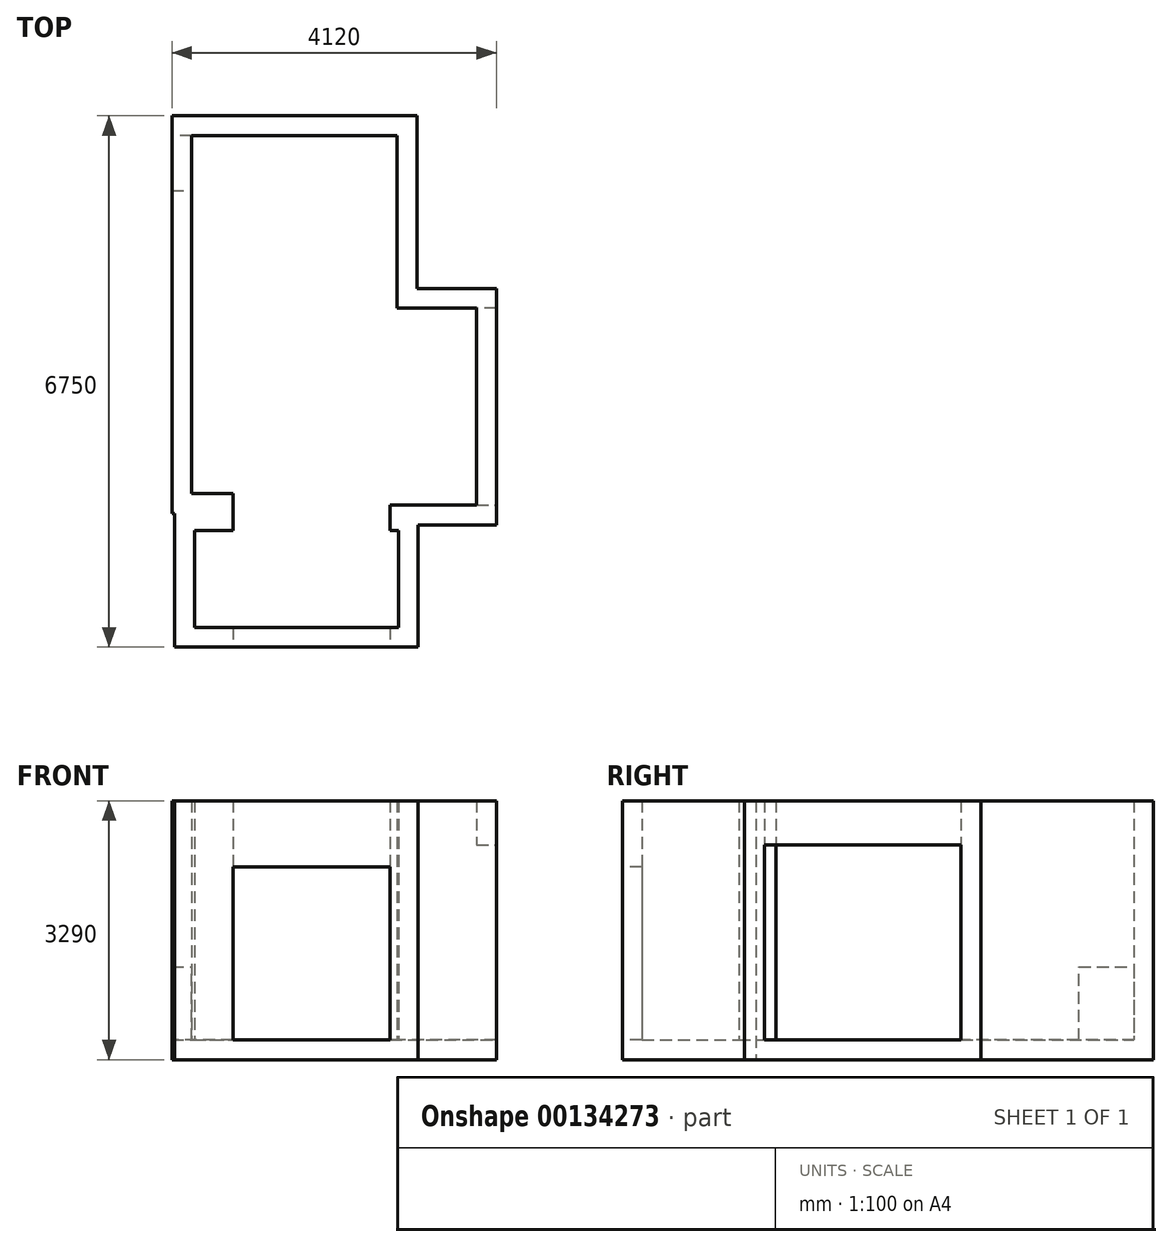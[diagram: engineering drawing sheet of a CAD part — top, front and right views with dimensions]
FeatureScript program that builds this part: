
annotation { "Feature Type Name" : "Feature", "Feature Type Description" : "" }
export const myFeature = defineFeature(function(context is Context, id is Id, definition is map)
    precondition{}
    {
        {
            var Q0;
            Q0=qCreatedBy(makeId("Top.planeOp"),FACE);
            var sketch = newSketch(context, id + "F0", { "sketchPlane" : qUnion([Q0])});
            skLineSegment(sketch, "E0", {"start": v(0, 0) * mm, "end": v(1649.99, 0) * mm});
            skLineSegment(sketch, "E1", {"start": v(1649.99, 0) * mm, "end": v(1649.99, 1230) * mm});
            skLineSegment(sketch, "E2", {"start": v(1649.99, 1230) * mm, "end": v(1544.99, 1230) * mm});
            skLineSegment(sketch, "E3", {"start": v(1544.99, 1230) * mm, "end": v(1544.99, 1555) * mm});
            skLineSegment(sketch, "E4", {"start": v(1544.99, 1555) * mm, "end": v(2644.99, 1555) * mm});
            skLineSegment(sketch, "E5", {"start": v(2644.99, 1555) * mm, "end": v(2644.99, 4055) * mm});
            skLineSegment(sketch, "E6", {"start": v(2644.99, 4055) * mm, "end": v(1634.99, 4055) * mm});
            skLineSegment(sketch, "E7", {"start": v(1634.99, 4055) * mm, "end": v(1634.99, 6250) * mm});
            skLineSegment(sketch, "E8", {"start": v(1634.99, 6250) * mm, "end": v(-975.01, 6250) * mm});
            skLineSegment(sketch, "E9", {"start": v(-975.01, 6250) * mm, "end": v(-975.01, 1700) * mm});
            skLineSegment(sketch, "E10", {"start": v(-975.01, 1700) * mm, "end": v(-450.01, 1700) * mm});
            skLineSegment(sketch, "E11", {"start": v(-450.01, 1700) * mm, "end": v(-450.01, 1230) * mm});
            skLineSegment(sketch, "E12", {"start": v(-450.01, 1230) * mm, "end": v(-940.01, 1230) * mm});
            skLineSegment(sketch, "E13", {"start": v(-940.01, 1230) * mm, "end": v(-940.01, 0) * mm});
            skLineSegment(sketch, "E14", {"start": v(-940.01, 0) * mm, "end": v(0, 0) * mm});
            skSolve(sketch);
        }
        {
            var Q0;
            Q0 = qSketchRegion(id + "F0", true);
            extrude(context, id + "F1", {"entities" : qUnion([Q0]), "depth" : 3040 * mm});
        }
        {
            var Q0;
            Q0=makeQuery(id+"F1.opExtrude","CAP_FACE",FACE,{"disambiguationData":[OSD([sQuery(id+"F0.wireOp",EDGE,"E0"),sQuery(id+"F0.wireOp",EDGE,"E1"),sQuery(id+"F0.wireOp",EDGE,"E2"),sQuery(id+"F0.wireOp",EDGE,"E3"),sQuery(id+"F0.wireOp",EDGE,"E4"),sQuery(id+"F0.wireOp",EDGE,"E5"),sQuery(id+"F0.wireOp",EDGE,"E6"),sQuery(id+"F0.wireOp",EDGE,"E7"),sQuery(id+"F0.wireOp",EDGE,"E8"),sQuery(id+"F0.wireOp",EDGE,"E9"),sQuery(id+"F0.wireOp",EDGE,"E10"),sQuery(id+"F0.wireOp",EDGE,"E11"),sQuery(id+"F0.wireOp",EDGE,"E12"),sQuery(id+"F0.wireOp",EDGE,"E13"),sQuery(id+"F0.wireOp",EDGE,"E14")])],"isStart":false});
            shell(context, id + "F2", {"entities" : qUnion([Q0]), "thickness" : 250 * mm, "oppositeDirection" : true});
        }
        {
            var Q0;
            Q0=makeQuery(id+"F2.opShell","OFFSET_FACE",FACE,{"disambiguationData":[OSD([sQuery(id+"F0.wireOp",EDGE,"E5")])]});
            var sketch = newSketch(context, id + "F3", { "sketchPlane" : qUnion([Q0])});
            skLineSegment(sketch, "E15.bottom", {"start": v(-3330, 1705) * mm, "end": v(-2620, 1705) * mm});
            skLineSegment(sketch, "E15.top", {"start": v(-3330, 980) * mm, "end": v(-2620, 980) * mm});
            skLineSegment(sketch, "E15.left", {"start": v(-3330, 1705) * mm, "end": v(-3330, 980) * mm});
            skLineSegment(sketch, "E15.right", {"start": v(-2620, 1705) * mm, "end": v(-2620, 980) * mm});
            skSolve(sketch);
        }
        {
            var Q0;
            Q0 = qSketchRegion(id + "F3", true);
            extrude(context, id + "F4", {"entities" : qUnion([Q0]), "operationType" : NewBodyOperationType.REMOVE, "endBound" : BoundingType.THROUGH_ALL, "oppositeDirection" : true, "depth" : 20 * mm});
        }
        {
            var Q0;
            Q0=makeQuery(id+"F1.opExtrude","SWEPT_FACE",FACE,{"disambiguationData":[OSD([sQuery(id+"F0.wireOp",EDGE,"E0"),sQuery(id+"F0.wireOp",EDGE,"E14")])]});
            var sketch = newSketch(context, id + "F5", { "sketchPlane" : qUnion([Q0])});
            skLineSegment(sketch, "E16.bottom", {"start": v(-450.01, 0) * mm, "end": v(1544.99, 0) * mm});
            skLineSegment(sketch, "E16.top", {"start": v(-450.01, 2200) * mm, "end": v(1544.99, 2200) * mm});
            skLineSegment(sketch, "E16.left", {"start": v(-450.01, 0) * mm, "end": v(-450.01, 2200) * mm});
            skLineSegment(sketch, "E16.right", {"start": v(1544.99, 0) * mm, "end": v(1544.99, 2200) * mm});
            skSolve(sketch);
        }
        {
            var Q0;
            Q0 = qSketchRegion(id + "F5", true);
            extrude(context, id + "F6", {"entities" : qUnion([Q0]), "operationType" : NewBodyOperationType.REMOVE, "oppositeDirection" : true, "depth" : 500 * mm});
        }
        {
            var Q0;
            Q0=makeQuery(id+"F2.opShell","OFFSET_FACE",FACE,{"disambiguationData":[OSD([sQuery(id+"F0.wireOp",EDGE,"E9")])]});
            var sketch = newSketch(context, id + "F7", { "sketchPlane" : qUnion([Q0])});
            skLineSegment(sketch, "E17.bottom", {"start": v(5550, 0) * mm, "end": v(6250, 0) * mm});
            skLineSegment(sketch, "E17.top", {"start": v(5550, 930) * mm, "end": v(6250, 930) * mm});
            skLineSegment(sketch, "E17.left", {"start": v(5550, 0) * mm, "end": v(5550, 930) * mm});
            skLineSegment(sketch, "E17.right", {"start": v(6250, 0) * mm, "end": v(6250, 930) * mm});
            skSolve(sketch);
        }
        {
            var Q0;
            Q0 = qSketchRegion(id + "F7", true);
            extrude(context, id + "F8", {"entities" : qUnion([Q0]), "operationType" : NewBodyOperationType.REMOVE, "endBound" : BoundingType.THROUGH_ALL, "oppositeDirection" : true, "depth" : 25 * mm});
        }
        {
            var Q0;
            Q0=makeQuery(id+"F1.opExtrude","SWEPT_FACE",FACE,{"disambiguationData":[OSD([sQuery(id+"F0.wireOp",EDGE,"E5")])]});
            var sketch = newSketch(context, id + "F9", { "sketchPlane" : qUnion([Q0])});
            skLineSegment(sketch, "E18.0", {"start": v(1555, 3040) * mm, "end": v(1555, 0) * mm});
            skLineSegment(sketch, "E19.0", {"start": v(4055, 3040) * mm, "end": v(4055, 0) * mm});
            skLineSegment(sketch, "E20.0", {"start": v(1555, 0) * mm, "end": v(4055, 0) * mm});
            skLineSegment(sketch, "E21.top", {"start": v(1555, 2480) * mm, "end": v(4055, 2480) * mm});
            skLineSegment(sketch, "E21.left", {"start": v(1555, 0) * mm, "end": v(1555, 2480) * mm});
            skLineSegment(sketch, "E21.right", {"start": v(4055, 0) * mm, "end": v(4055, 2480) * mm});
            skSolve(sketch);
        }
        {
            var Q0;
            Q0=makeQuery(id+"F9.imprint","IMPRINT",FACE,{"disambiguationData":[TD([[makeQuery(id+"F9.imprint","IMPRINT",EDGE,{"derivedFrom":sQuery(id+"F9.wireOp",EDGE,"E20.0")}),1.0]])]});
            extrude(context, id + "F10", {"entities" : qUnion([Q0]), "operationType" : NewBodyOperationType.REMOVE, "endBound" : BoundingType.UP_TO_NEXT, "oppositeDirection" : true, "depth" : 25 * mm});
        }
    });
